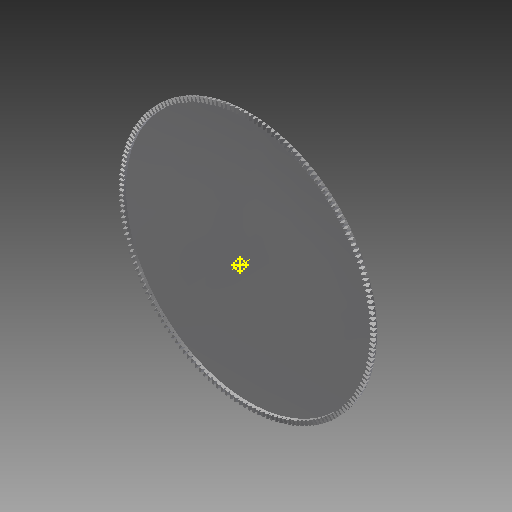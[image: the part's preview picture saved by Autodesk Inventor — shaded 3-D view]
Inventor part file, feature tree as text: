
AUTODESK INVENTOR PART (.ipt)
format: ipt  version: 2017 (Build 210142000, 142)  size: 2,374,656 bytes
history: native  units: mm
features: other x24, loft x2, pattern_circular x2, sketch x1
ambient origin geometry x6: Origin, XZ Plane, X Axis, Y Axis, Z Axis, Center Point
bodies: Solid1 (feature_tree)
feature tree (29):
  other  "Top Point"
  other  "Mesh Plane2"
  other  "Teeth Body"
  other  "Start Point"
  other  "Tooth Plane"
  other  "Start Sketch"
  other  "End Point"
  other  "3D Sketch Right"
  other  "End Plane Right"
  loft  "Loft Right"
  pattern_circular  "Circular Pattern Right"  [2 undecoded]
  other  "3D Sketch Left"
  other  "End Plane Left"
  loft  "Loft Left"
  pattern_circular  "Circular Pattern Left"  [2 undecoded]
  other  "Fix Body"
  other  "Mesh Plane"
  other  "Top Plane"
  other  "Teeth Body Sketch"
  other  "End Plane"
  other  "End Sketch"
  other  "Helical Curve Left"
  other  "End Sketch Left"
  other  "Body Sketch"
  sketch  "Sketch6"  dims[d0=298.026667mm d1=297.721421mm d2=298.228244mm d3=5.08mm d4=8.681765mm d5=90.0deg d7=925.768798mm d8=848.473196mm d9=1817.033254mm d11=5.266267mm d12=894.052839mm d15=819.405312mm d16=1754.783423mm d17=0.0mm d18=90.0deg d19=0.0mm d20=90.0deg d21=1760.0mm d22=360.0deg d26=126.354884mm d27=0.358232mm d28=298.026667mm d29=-15.027199mm d30=894.052839mm d31=819.405312mm d32=1754.783423mm d35=0.0mm d37=0.0mm d39=0.0mm d40=90.0deg d41=1760.0mm d42=360.0deg d46=90.0deg d47=90.0deg d48=0.0mm d49=0.0mm d50=90.0deg d51=0.1785mm d52=0.0mm d53=0.0mm d54=0.0mm d56=9.853856mm d57=2193.202266mm d58=2187.912293mm d59=2118.065243mm d60=2112.956499mm d61=2118.065243mm d62=2112.956499mm d63=90.0deg d64=90.0deg d65=126.354884mm d66=31.5mm d67=298.026667mm d68=-15.027199mm d69=0.358232mm d70=819.405312mm d71=1754.783423mm d72=894.052839mm d73=2112.956499mm d74=2118.065243mm d75=0.0mm d76=90.0deg d77=0.0mm d78=90.0deg d79=0.0mm d80=90.0deg d81=1760.0mm d82=360.0deg d84=10.0mm d85=20.0mm d86=20.0mm d87=10.0mm d88=0.0mm d89=0.0mm]
  other  "Srf1"
  other  "Helical Curve Right"
  other  "End Sketch Right"
  other  "Pitch Diameter"
note: 4 required parameter values undecoded (feature->parameter linkage not recoverable at this tier; creation-order binding heuristic only, values carry confidence <= 0.55)
